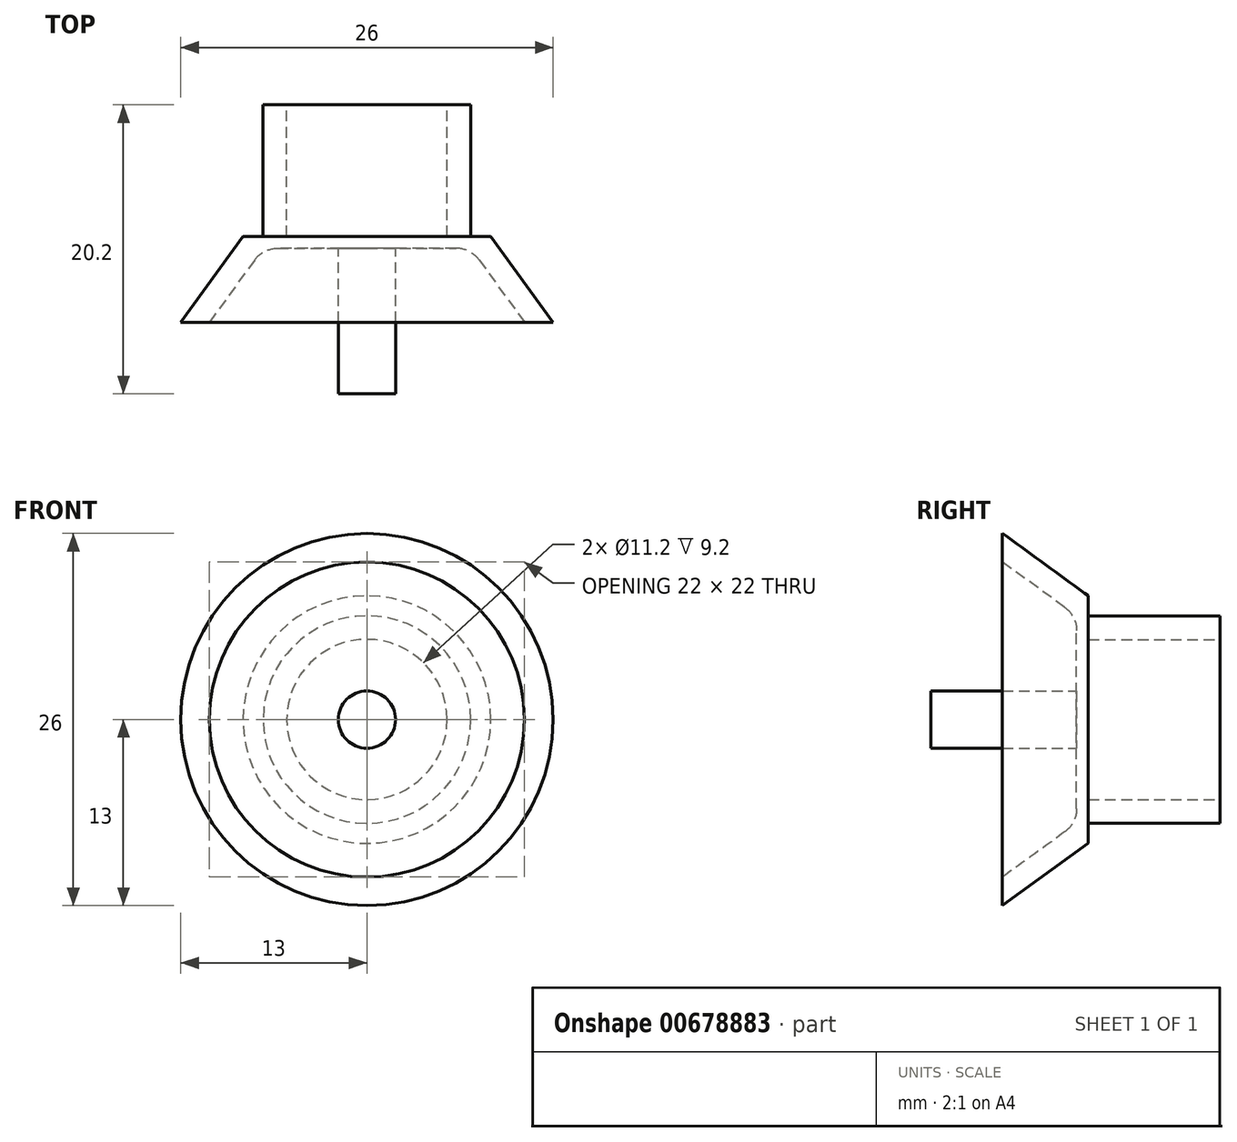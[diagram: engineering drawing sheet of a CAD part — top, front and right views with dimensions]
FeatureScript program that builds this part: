
annotation { "Feature Type Name" : "Feature", "Feature Type Description" : "" }
export const myFeature = defineFeature(function(context is Context, id is Id, definition is map)
    precondition{}
    {
        {
            var Q0;
            Q0=qCreatedBy(makeId("Right.planeOp"),FACE);
            var sketch = newSketch(context, id + "F0", { "sketchPlane" : qUnion([Q0])});
            skLineSegment(sketch, "E0", {"start": v(0, 0) * mm, "end": v(0, 5.6) * mm});
            skLineSegment(sketch, "E1", {"start": v(0, 5.6) * mm, "end": v(9.2, 5.6) * mm});
            skLineSegment(sketch, "E2", {"start": v(9.2, 5.6) * mm, "end": v(9.2, 7.25) * mm});
            skLineSegment(sketch, "E3", {"start": v(9.2, 7.25) * mm, "end": v(0, 7.25) * mm});
            skLineSegment(sketch, "E4", {"start": v(0, 7.25) * mm, "end": v(0, 8.65) * mm});
            skLineSegment(sketch, "E5", {"start": v(0, 8.65) * mm, "end": v(-6, 13) * mm});
            skLineSegment(sketch, "E6", {"start": v(-6, 13) * mm, "end": v(-6, 11) * mm});
            skLineSegment(sketch, "E7", {"start": v(-6, 11) * mm, "end": v(-0.83, 7.25) * mm});
            skLineSegment(sketch, "E8", {"start": v(-0.83, 7.25) * mm, "end": v(-0.83, 2) * mm});
            skLineSegment(sketch, "E9", {"start": v(-0.83, 2) * mm, "end": v(-11, 2) * mm});
            skLineSegment(sketch, "E10", {"start": v(-11, 2) * mm, "end": v(-11, 0) * mm});
            skLineSegment(sketch, "E11", {"start": v(-11, 0) * mm, "end": v(0, 0) * mm});
            skSolve(sketch);
        }
        {
            var Q0;
            Q0=qCreatedBy(makeId("Right.planeOp"),FACE);
            var sketch = newSketch(context, id + "F1", { "sketchPlane" : qUnion([Q0])});
            skLineSegment(sketch, "E12", {"start": v(53.9, 0) * mm, "end": v(-60.83, 0) * mm});
            skSolve(sketch);
        }
        {
            var Q0;
            Q0=makeQuery(id+"F0.imprint","IMPRINT",FACE,{"disambiguationData":[TD([[makeQuery(id+"F0.imprint","IMPRINT",EDGE,{"derivedFrom":sQuery(id+"F0.wireOp",EDGE,"E0")}),1.0]])]});
            var Q1;
            Q1=sQuery(id+"F1.wireOp",EDGE,"E12");
            revolve(context, id + "F2", {"entities" : qUnion([Q0]), "axis" : qUnion([Q1]), "revolveType" : RevolveType.FULL});
        }
        {
            var Q0;
            Q0=makeQuery(id+"F2.opRevolve","SWEPT_EDGE",EDGE,{"disambiguationData":[OSD([sQuery(id+"F0.wireOp",EDGE,"E7"),sQuery(id+"F0.wireOp",EDGE,"E8")])]});
            fillet(context, id + "F3", {"entities" : qUnion([Q0]), "radius" : 2 * mm, "tangentPropagation" : true, "allowEdgeOverflow" : false});
        }
        {
            var Q0;
            Q0=makeQuery(id+"F2.opRevolve","SWEPT_BODY",BODY,{"disambiguationData":[OSD([sQuery(id+"F0.wireOp",EDGE,"E0"),sQuery(id+"F0.wireOp",EDGE,"E1"),sQuery(id+"F0.wireOp",EDGE,"E2"),sQuery(id+"F0.wireOp",EDGE,"E3"),sQuery(id+"F0.wireOp",EDGE,"E4"),sQuery(id+"F0.wireOp",EDGE,"E5"),sQuery(id+"F0.wireOp",EDGE,"E6"),sQuery(id+"F0.wireOp",EDGE,"E7"),sQuery(id+"F0.wireOp",EDGE,"E8"),sQuery(id+"F0.wireOp",EDGE,"E9"),sQuery(id+"F0.wireOp",EDGE,"E10"),sQuery(id+"F0.wireOp",EDGE,"E11")])]});
            transform(context, id + "F4", {"entities" : qUnion([Q0]), "transformType" : TransformType.TRANSLATION_3D, "dx" : 0 * mm, "dy" : 0 * mm, "dz" : 0 * mm, "makeCopy" : true});
        }
    });
